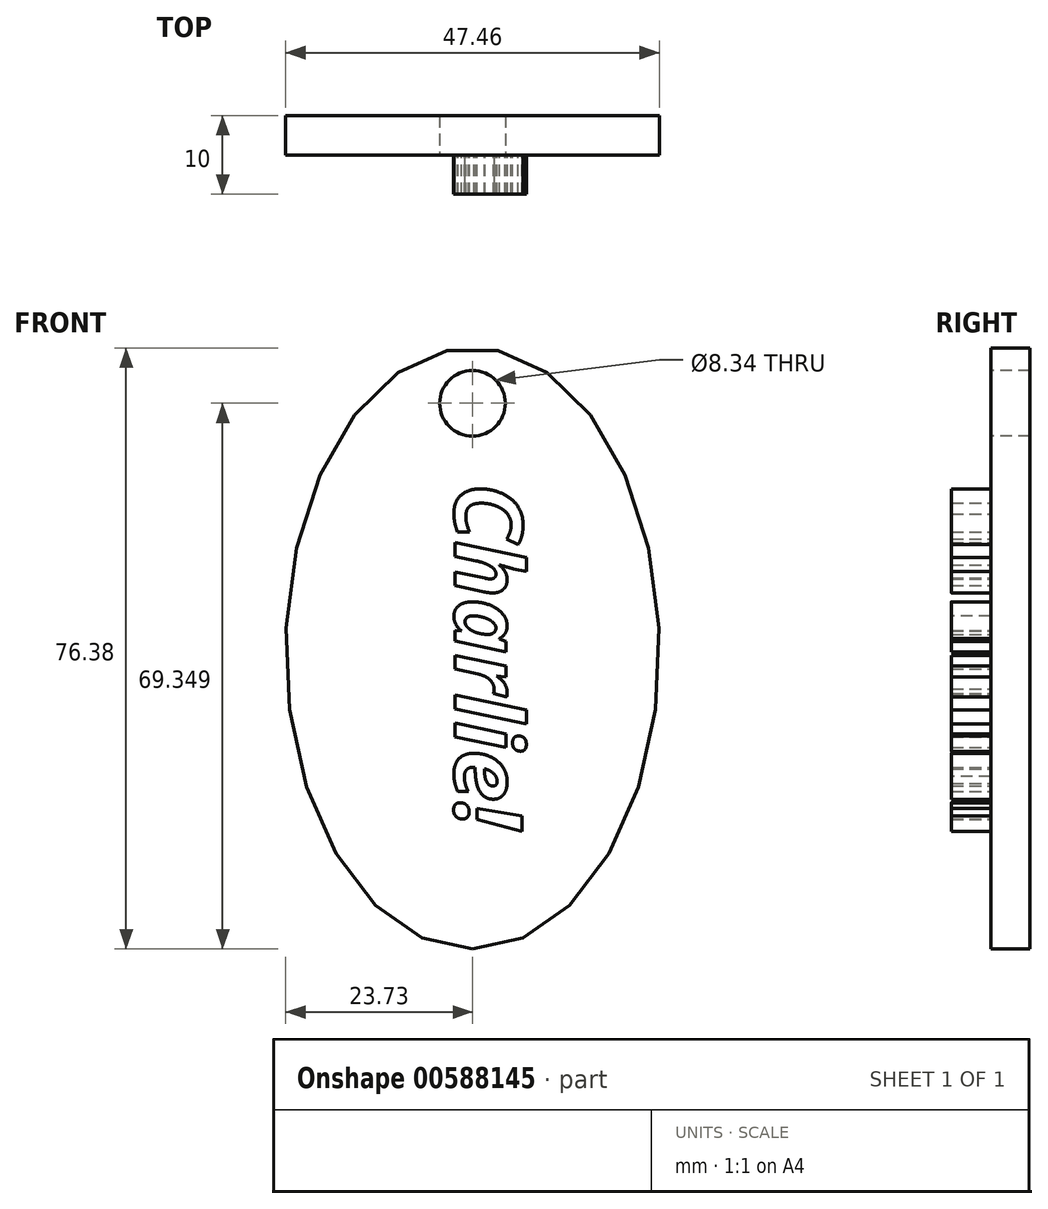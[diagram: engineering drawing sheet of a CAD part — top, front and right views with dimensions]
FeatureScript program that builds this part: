
annotation { "Feature Type Name" : "Feature", "Feature Type Description" : "" }
export const myFeature = defineFeature(function(context is Context, id is Id, definition is map)
    precondition{}
    {
        {
            var Q0;
            Q0=qCreatedBy(makeId("Front.planeOp"),FACE);
            var sketch = newSketch(context, id + "F0", { "sketchPlane" : qUnion([Q0])});
            skEllipse(sketch, "E0", {"center": v(0, 38.2) * mm, "majorRadius": 38.2 * mm, "minorRadius": 23.73 * mm, "majorAxis": v(0, -1)});
            skSolve(sketch);
        }
        {
            var Q0;
            Q0=makeQuery(id+"F0.imprint","IMPRINT",FACE,{"disambiguationData":[TD([[makeQuery(id+"F0.imprint","IMPRINT",EDGE,{"derivedFrom":sQuery(id+"F0.wireOp",EDGE,"E0")}),1.0]])]});
            extrude(context, id + "F1", {"entities" : qUnion([Q0]), "depth" : 5 * mm, "offsetDistance" : 25.4 * mm});
        }
        {
            var Q0;
            Q0=makeQuery(id+"F1.opExtrude","CAP_FACE",FACE,{"disambiguationData":[OSD([sQuery(id+"F0.wireOp",EDGE,"E0")])],"isStart":false});
            var sketch = newSketch(context, id + "F2", { "sketchPlane" : qUnion([Q0])});
            skCircle(sketch, "E1", {"center": v(0, 69.35) * mm, "radius": 4.17 * mm});
            skSolve(sketch);
        }
        {
            var Q0;
            Q0=makeQuery(id+"F2.imprint","IMPRINT",FACE,{"disambiguationData":[TD([[makeQuery(id+"F2.imprint","IMPRINT",EDGE,{"derivedFrom":sQuery(id+"F2.wireOp",EDGE,"E1")}),1.0]])]});
            extrude(context, id + "F3", {"entities" : qUnion([Q0]), "operationType" : NewBodyOperationType.REMOVE, "endBound" : BoundingType.THROUGH_ALL, "oppositeDirection" : true, "depth" : 10 * mm, "offsetDistance" : 25 * mm});
        }
        {
            var Q0;
            Q0=makeQuery(id+"F1.opExtrude","CAP_FACE",FACE,{"disambiguationData":[OSD([sQuery(id+"F0.wireOp",EDGE,"E0")])],"isStart":false});
            var sketch = newSketch(context, id + "F4", { "sketchPlane" : qUnion([Q0])});
            skText(sketch, "E2", { "text": "Charlie!", "fontName": "OpenSans-BoldItalic.ttf"});
            const initialGuessF4  = {"E2": [-0.00225, 0.05918, 0, -1, 0.00861]};
            skSetInitialGuess(sketch, initialGuessF4);
            skSolve(sketch);
        }
        {
            var Q0;
            Q0 = qSketchRegion(id + "F4", true);
            extrude(context, id + "F5", {"entities" : qUnion([Q0]), "operationType" : NewBodyOperationType.ADD, "depth" : 5 * mm, "offsetDistance" : 25 * mm});
        }
    });
